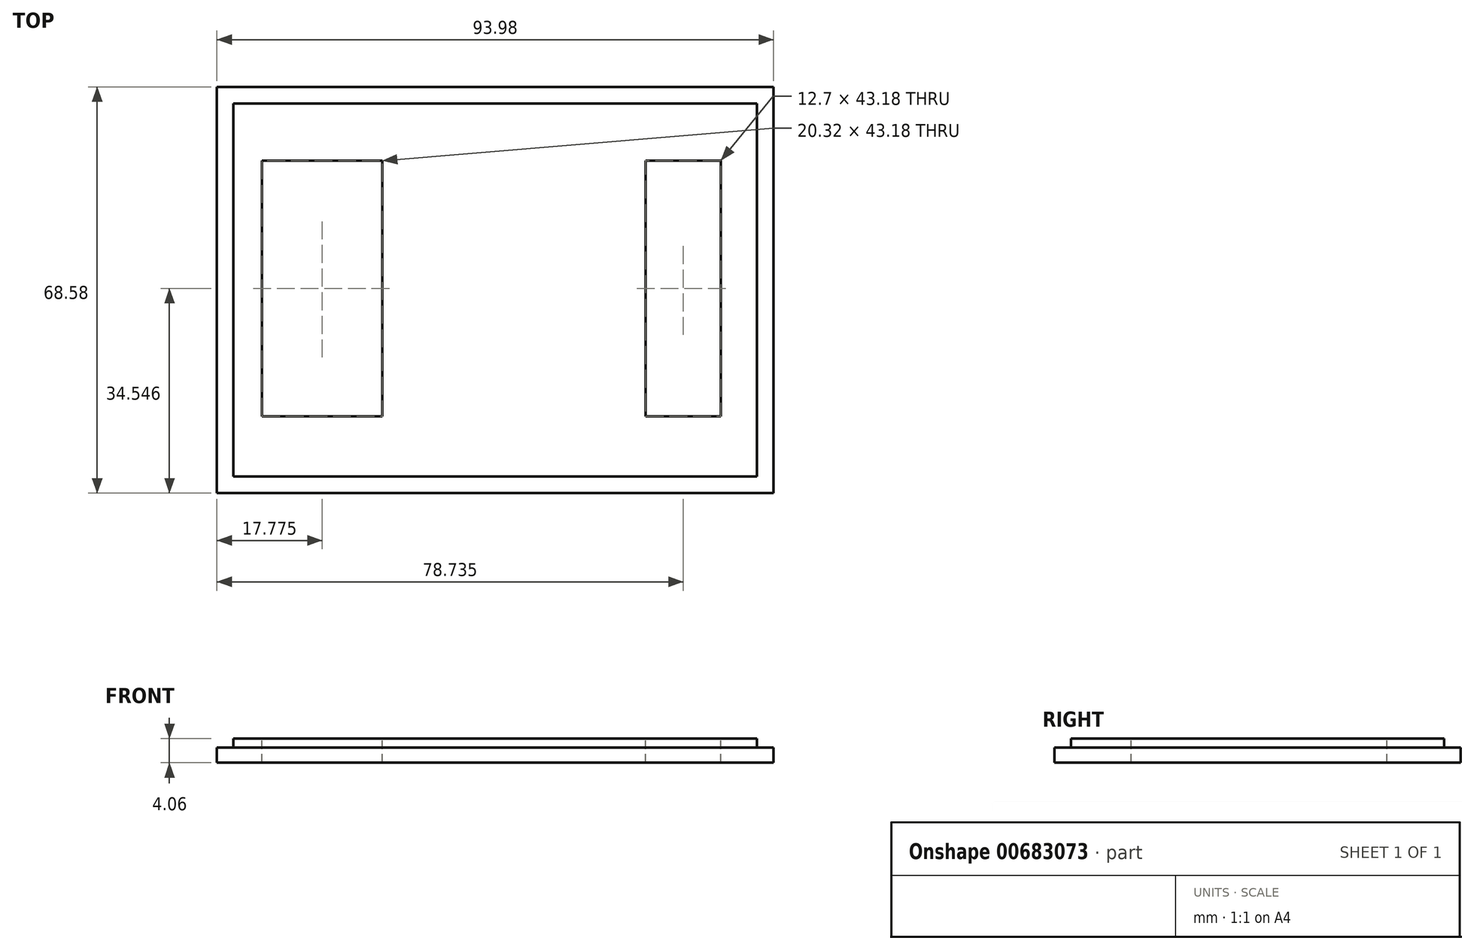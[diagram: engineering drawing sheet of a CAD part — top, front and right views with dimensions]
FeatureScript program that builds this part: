
annotation { "Feature Type Name" : "Feature", "Feature Type Description" : "" }
export const myFeature = defineFeature(function(context is Context, id is Id, definition is map)
    precondition{}
    {
        {
            var Q0;
            Q0=qCreatedBy(makeId("Top.planeOp"),FACE);
            var sketch = newSketch(context, id + "F0", { "sketchPlane" : qUnion([Q0])});
            skLineSegment(sketch, "E0.bottom", {"start": v(-48.14, 19.52) * mm, "end": v(45.84, 19.52) * mm});
            skLineSegment(sketch, "E0.top", {"start": v(-48.14, -49.06) * mm, "end": v(45.84, -49.06) * mm});
            skLineSegment(sketch, "E0.left", {"start": v(-48.14, 19.52) * mm, "end": v(-48.14, -49.06) * mm});
            skLineSegment(sketch, "E0.right", {"start": v(45.84, 19.52) * mm, "end": v(45.84, -49.06) * mm});
            skSolve(sketch);
        }
        {
            var Q0;
            Q0=makeQuery(id+"F0.imprint","IMPRINT",FACE,{"disambiguationData":[TD([[makeQuery(id+"F0.imprint","IMPRINT",EDGE,{"derivedFrom":sQuery(id+"F0.wireOp",EDGE,"E0.bottom")}),-1.0]])]});
            var Q1;
            Q1=makeQuery(id+"F0.imprint","IMPRINT",FACE,{"disambiguationData":[TD([[makeQuery(id+"F0.imprint","IMPRINT",EDGE,{"derivedFrom":sQuery(id+"F0.wireOp",EDGE,"pFGV6UEe-QcPB-FiE4-hveY-gTO97t8oy3bb.bottom")}),-1.0]])]});
            extrude(context, id + "F1", {"entities" : qUnion([Q0, Q1]), "depth" : 2.54 * mm, "offsetDistance" : 25.4 * mm});
        }
        {
            var Q0;
            Q0=makeQuery(id+"F1.opExtrude","CAP_FACE",FACE,{"disambiguationData":[OSD([sQuery(id+"F0.wireOp",EDGE,"E0.bottom"),sQuery(id+"F0.wireOp",EDGE,"E0.top"),sQuery(id+"F0.wireOp",EDGE,"E0.left"),sQuery(id+"F0.wireOp",EDGE,"E0.right")])],"isStart":false});
            var sketch = newSketch(context, id + "F2", { "sketchPlane" : qUnion([Q0])});
            skLineSegment(sketch, "E1.bottom", {"start": v(-45.35, 16.73) * mm, "end": v(43.04, 16.73) * mm});
            skLineSegment(sketch, "E1.top", {"start": v(-45.35, -46.26) * mm, "end": v(43.04, -46.26) * mm});
            skLineSegment(sketch, "E1.left", {"start": v(-45.35, 16.73) * mm, "end": v(-45.35, -46.26) * mm});
            skLineSegment(sketch, "E1.right", {"start": v(43.04, 16.73) * mm, "end": v(43.04, -46.26) * mm});
            skSolve(sketch);
        }
        {
            var Q0;
            Q0 = qSketchRegion(id + "F2", true);
            extrude(context, id + "F3", {"entities" : qUnion([Q0]), "operationType" : NewBodyOperationType.ADD, "depth" : 1.52 * mm, "offsetDistance" : 25.4 * mm});
        }
        {
            var Q0;
            Q0=makeQuery(id+"F3.opExtrude","CAP_FACE",FACE,{"disambiguationData":[OSD([sQuery(id+"F2.wireOp",EDGE,"E1.bottom"),sQuery(id+"F2.wireOp",EDGE,"E1.top"),sQuery(id+"F2.wireOp",EDGE,"E1.left"),sQuery(id+"F2.wireOp",EDGE,"E1.right")])],"isStart":false});
            var sketch = newSketch(context, id + "F4", { "sketchPlane" : qUnion([Q0])});
            skLineSegment(sketch, "E2.bottom", {"start": v(24.25, 7.08) * mm, "end": v(36.95, 7.08) * mm});
            skLineSegment(sketch, "E2.top", {"start": v(24.25, -36.1) * mm, "end": v(36.95, -36.1) * mm});
            skLineSegment(sketch, "E2.left", {"start": v(24.25, 7.08) * mm, "end": v(24.25, -36.1) * mm});
            skLineSegment(sketch, "E2.right", {"start": v(36.95, 7.08) * mm, "end": v(36.95, -36.1) * mm});
            skSolve(sketch);
        }
        {
            var Q0;
            Q0=makeQuery(id+"F4.imprint","IMPRINT",FACE,{"disambiguationData":[TD([[makeQuery(id+"F4.imprint","IMPRINT",EDGE,{"derivedFrom":sQuery(id+"F4.wireOp",EDGE,"E2.bottom")}),-1.0]])]});
            extrude(context, id + "F5", {"entities" : qUnion([Q0]), "operationType" : NewBodyOperationType.REMOVE, "endBound" : BoundingType.THROUGH_ALL, "oppositeDirection" : true, "depth" : 25.4 * mm, "offsetDistance" : 25.4 * mm});
        }
        {
            var Q0;
            Q0=makeQuery(id+"F3.opExtrude","CAP_FACE",FACE,{"disambiguationData":[OSD([sQuery(id+"F2.wireOp",EDGE,"E1.bottom"),sQuery(id+"F2.wireOp",EDGE,"E1.top"),sQuery(id+"F2.wireOp",EDGE,"E1.left"),sQuery(id+"F2.wireOp",EDGE,"E1.right")])],"isStart":false});
            var sketch = newSketch(context, id + "F6", { "sketchPlane" : qUnion([Q0])});
            skLineSegment(sketch, "E3.bottom", {"start": v(-40.52, 7.08) * mm, "end": v(-20.2, 7.08) * mm});
            skLineSegment(sketch, "E3.top", {"start": v(-40.52, -36.1) * mm, "end": v(-20.2, -36.1) * mm});
            skLineSegment(sketch, "E3.left", {"start": v(-40.52, 7.08) * mm, "end": v(-40.52, -36.1) * mm});
            skLineSegment(sketch, "E3.right", {"start": v(-20.2, 7.08) * mm, "end": v(-20.2, -36.1) * mm});
            skSolve(sketch);
        }
        {
            var Q0;
            Q0 = qSketchRegion(id + "F6", true);
            extrude(context, id + "F7", {"entities" : qUnion([Q0]), "operationType" : NewBodyOperationType.REMOVE, "endBound" : BoundingType.THROUGH_ALL, "oppositeDirection" : true, "depth" : 25.4 * mm, "offsetDistance" : 25.4 * mm});
        }
    });
